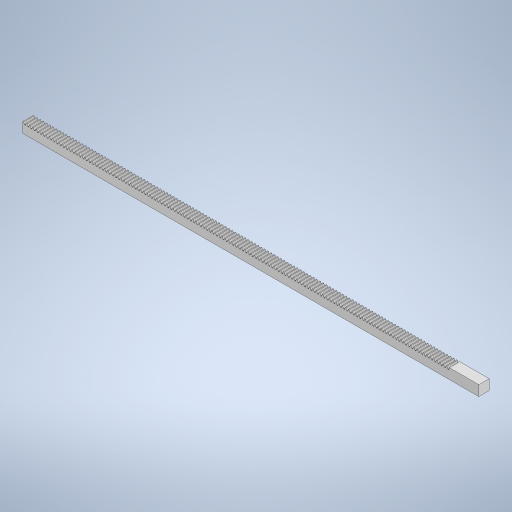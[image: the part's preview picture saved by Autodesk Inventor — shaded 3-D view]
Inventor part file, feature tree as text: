
AUTODESK INVENTOR PART (.ipt)
format: ipt  version: 2023 (Build 270158000, 158)  size: 1,240,576 bytes
history: mixed  units: in
note: dims shown in document units (in); Inventor stores cm internally (conversion verified against a paired STEP export)
features: extrude x1, sketch x1, other x1, imported_body x1
ambient origin geometry x8: Origin, YZ Plane, XZ Plane, XY Plane, X Axis, Y Axis, Z Axis, Center Point
bodies: Solid1 (imported_parasolid)
feature tree (4):
  extrude  "Extrusion1"  Depth=0.3937in
  sketch  "Sketch1"  dims[d0=0.0332in d1=0.0864in d2=0.0082in d3=0.0159in d4=0.0082in d6=0.0082in d7=0.0082in d8=0.0159in d9=0.0082in d10=0.0905in d11=0.7734in d12=0.7734in d117=5.3228in d391=0.0in d392=0.0332in d393=0.0864in d394=0.0082in d395=0.0159in d396=0.0082in d397=0.0082in d398=0.0082in d399=0.0159in d400=0.0082in d401=0.0905in d402=0.7734in d403=0.7734in d404=0.0in d405=0.0332in d406=0.0864in d407=0.0082in d408=0.0159in d409=0.0082in d410=0.0082in d411=0.0082in d412=0.0159in d413=0.0082in d414=0.0905in d415=0.7734in d416=0.7734in d417=0.0in d418=0.0332in d419=0.0864in d420=0.0082in d421=0.0159in d422=0.0082in d423=0.0082in d424=0.0082in d425=0.0159in d426=0.0082in d427=0.0905in d428=0.7734in d429=0.7734in d430=0.0in d431=0.0332in d432=0.0864in d433=0.0082in d434=0.0159in d435=0.0082in d436=0.0082in d437=0.0082in d438=0.0159in d439=0.0082in d440=0.0905in d441=0.7734in d442=0.7734in d443=0.0in d444=0.0332in d445=0.0864in d446=0.0082in d447=0.0159in d448=0.0082in d449=0.0082in d450=0.0082in d451=0.0159in d452=0.0082in d453=0.0905in d454=0.7734in d455=0.7734in d456=0.0in d457=0.0332in d458=0.0864in d459=0.0082in d460=0.0159in d461=0.0082in d462=0.0082in d463=0.0082in d464=0.0159in d465=0.0082in d466=0.0905in d467=0.7734in d468=0.7734in d469=0.0in d470=0.0332in d471=0.0864in d472=0.0082in d473=0.0159in d474=0.0082in d475=0.0082in d476=0.0082in d477=0.0159in d478=0.0082in d479=0.0905in d480=0.7734in d481=0.7734in d482=0.0in d483=0.0332in d484=0.0864in d485=0.0082in d486=0.0159in d487=0.0082in d488=0.0082in d489=0.0082in d490=0.0159in d491=0.0082in d492=0.0905in d493=0.7734in d494=0.7734in d495=0.0in d496=0.0332in d497=0.0864in d498=0.0082in d499=0.0159in d500=0.0082in d501=0.0082in d502=0.0082in d503=0.0159in d504=0.0082in d505=0.0905in d506=0.7734in d507=0.7734in d508=0.0in d509=0.0332in d510=0.0864in d511=0.0082in d512=0.0159in d513=0.0082in d514=0.0082in d515=0.0082in d516=0.0159in d517=0.0082in d518=0.0905in d519=0.7734in d520=0.7734in d521=0.0in d522=0.0332in d523=0.0864in d524=0.0082in d525=0.0159in d526=0.0082in d527=0.0082in d528=0.0082in d529=0.0159in d530=0.0082in d531=0.0905in d532=0.7734in d533=0.7734in d534=0.0in d535=0.0332in d536=0.0864in d537=0.0082in d538=0.0159in d539=0.0082in d540=0.0082in d541=0.0082in d542=0.0159in d543=0.0082in d544=0.0905in d545=0.7734in d546=0.7734in d547=0.0in d548=0.0332in d549=0.0864in d550=0.0082in d551=0.0159in d552=0.0082in d553=0.0082in d554=0.0082in d555=0.0159in d556=0.0082in d557=0.0905in d558=0.7734in d559=0.7734in d560=0.0in d561=0.0332in d562=0.0864in d563=0.0082in d564=0.0159in d565=0.0082in d566=0.0082in d567=0.0082in d568=0.0159in d569=0.0082in d570=0.0905in d571=0.7734in d572=0.7734in d573=0.0in d574=0.0332in d575=0.0864in d576=0.0082in d577=0.0159in d578=0.0082in d579=0.0082in d580=0.0082in d581=0.0159in d582=0.0082in d583=0.0905in d584=0.7734in d585=0.7734in d586=0.0in d587=0.0332in d588=0.0864in d589=0.0082in d590=0.0159in d591=0.0082in d592=0.0082in d593=0.0082in d594=0.0159in d595=0.0082in d596=0.0905in d597=0.7734in d598=0.7734in d599=0.0in d600=0.0332in d601=0.0864in d602=0.0082in d603=0.0159in d604=0.0082in d605=0.0082in d606=0.0082in d607=0.0159in d608=0.0082in d609=0.0905in d610=0.7734in d611=0.7734in d612=0.0in d613=0.0332in d614=0.0864in d615=0.0082in d616=0.0159in d617=0.0082in d618=0.0082in d619=0.0082in d620=0.0159in d621=0.0082in d622=0.0905in d623=0.7734in d624=0.7734in d625=0.0in d626=0.0332in d627=0.0864in d628=0.0082in d629=0.0159in d630=0.0082in d631=0.0082in d632=0.0082in d633=0.0159in d634=0.0082in d635=0.0905in d636=0.7734in d637=0.7734in d638=0.0in d639=0.0332in d640=0.0864in d641=0.0082in d642=0.0159in d643=0.0082in d644=0.0082in d645=0.0082in d646=0.0159in d647=0.0082in d648=0.0905in d649=0.7734in d650=0.7734in d651=0.0in d652=0.0332in d653=0.0864in d654=0.0082in d655=0.0159in d656=0.0082in d657=0.0082in d658=0.0082in d659=0.0159in d660=0.0082in d661=0.0905in d662=0.7734in d663=0.7734in d664=0.0in d665=0.0332in d666=0.0864in d667=0.0082in d668=0.0159in d669=0.0082in d670=0.0082in d671=0.0082in d672=0.0159in d673=0.0082in d674=0.0905in d675=0.7734in d676=0.7734in d677=0.0in d678=0.0332in d679=0.0864in d680=0.0082in d681=0.0159in d682=0.0082in d683=0.0082in d684=0.0082in d685=0.0159in d686=0.0082in d687=0.0905in d688=0.7734in d689=0.7734in d690=0.0in d691=0.0332in d692=0.0864in d693=0.0082in d694=0.0159in d695=0.0082in d696=0.0082in d697=0.0082in d698=0.0159in d699=0.0082in d700=0.0905in d701=0.7734in d702=0.7734in d703=0.0in d704=0.0332in d705=0.0864in d706=0.0082in d707=0.0159in d708=0.0082in d709=0.0082in d710=0.0082in d711=0.0159in d712=0.0082in d713=0.0905in d714=0.7734in d715=0.7734in d716=0.0in d717=0.0332in d718=0.0864in d719=0.0082in d720=0.0159in d721=0.0082in d722=0.0082in d723=0.0082in d724=0.0159in d725=0.0082in d726=0.0905in d727=0.7734in d728=0.7734in d729=0.0in d730=0.0332in d731=0.0864in d732=0.0082in d733=0.0159in d734=0.0082in d735=0.0082in d736=0.0082in d737=0.0159in d738=0.0082in d739=0.0905in d740=0.7734in d741=0.7734in d742=0.0in d743=0.0332in d744=0.0864in d745=0.0082in d746=0.0159in d747=0.0082in d748=0.0082in d749=0.0082in d750=0.0159in d751=0.0082in d752=0.0905in d753=0.7734in d754=0.7734in d755=0.0in d756=0.0332in d757=0.0864in d758=0.0082in d759=0.0159in d760=0.0082in d761=0.0082in d762=0.0082in d763=0.0159in d764=0.0082in d765=0.0905in d766=0.7734in d767=0.7734in d768=0.0in d769=0.0332in d770=0.0864in d771=0.0082in d772=0.0159in d773=0.0082in d774=0.0082in d775=0.0082in d776=0.0159in d777=0.0082in d778=0.0905in d779=0.7734in d780=0.7734in d781=0.0in d782=0.0332in d783=0.0864in d784=0.0082in d785=0.0159in d786=0.0082in d787=0.0082in d788=0.0082in d789=0.0159in d790=0.0082in d791=0.0905in d792=0.7734in d793=0.7734in d794=0.0in d795=0.0332in d796=0.0864in d797=0.0082in d798=0.0159in d799=0.0082in d800=0.0082in d801=0.0082in d802=0.0159in d803=0.0082in d804=0.0905in d805=0.7734in d806=0.7734in d807=0.0in d808=0.0332in d809=0.0864in d810=0.0082in d811=0.0159in d812=0.0082in d813=0.0082in d814=0.0082in d815=0.0159in d816=0.0082in d817=0.0905in d818=0.7734in d819=0.7734in d820=0.0in d847=0.3937in d848=0.0in]
  other  "LPattern1"
  imported_body  NMx_Import_Brep_tag  [imported B-rep: ~792 faces, bbox_mm=[440.0, 10.0, 10.0]]
